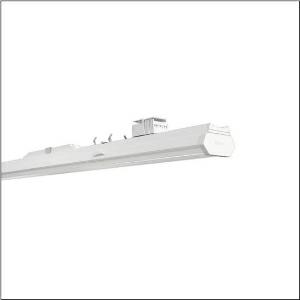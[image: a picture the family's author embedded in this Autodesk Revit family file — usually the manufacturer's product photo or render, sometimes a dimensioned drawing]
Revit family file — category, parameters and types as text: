
# Revit family: licross_r__11_protected_ho_51td12dn4fxm3s_901f
name_source: partatom
category: Lighting Fixtures
units: mm (PartAtom-declared; Revit-internal decimal feet)

## family parameters
Cut with Voids When Loaded = No
Host = Face
Light Source = No
Part Type = Normal
Room Calculation Point = No
Round Connector Dimension = Use Diameter
Shared = No

## types (1)
- --- (1 x LED, 970 lm, 7.4 W, 4000K)
    Apparent Load = 7 VA
    CIE Flux Codes = 70 91 97 98 100
    Color Rendering = 80
    Color Temperature = 4000K
    Default Elevation = 1800 mm
    Description = Licross® 11 Protected HO, luminaire insert, of sheet steel, galvanised, coil coated, white, length: 1.500mm, width: 90mm, height: 101mm, LED rated luminous flux: 15.270lm, light colour: 840, control gear: DALI 2 (for two DALI lines), with plug, 6-pole, with phase selection, for trunking rail, 14-core, mains connection: 220..240V, AC, 50/60Hz, rated input power: 91W, for trunking rail, 14-core, halogen-free wiring, for emergency light function, converter,control gear: single battery element, battery: LiFePO4, 9Ah, primary light control with lens, of plastic, primary optical cover: cover, of PMMA, light emission: direct distribution, primary light characteristic: symmetric, protection rating (complete): IP54, insulation class (complete): insulation class I (protective earthing), certification: CE, UKCA, protection symbol: D if used in an environment with non-conductive dust loads with corresponding accessories, impact resistance: IK06, permissible ambient temperature for indoor applications: +5..+30°C, standard: EN 60598-2-22, LABS conformity tested according to VDMA 24364:2018-05, reducing of maximum allowable ambient temperature of 5°C with ceiling mounting, corresponds to IFS (International Featured Standards) requirements for safety and quality in the food industry, packaging unit: 1 piece
    Height = 92 mm
    Lamp = 1 x LED
    Lamp Light Flux = 970 lm
    Lamp Power = 7.4 W
    Lamp count = 1
    Length = 1500 mm
    Luminous efficacy = 131 lm/W
    Manufacturer = Siteco
    ModVariant = No
    Model = 51TD12DN4FXM3S
    Mounting Place = Ceiling
    Mounting Type = Pendant
    Number of Poles = 1
    OnlyDefault = Yes
    Power Factor = 1
    Product Name = Licross® 11 Protected HO
    Product group = luminaire insert
    ProductGroupID = 902
    Protection Class = Protection class I
    Protection Degree = IP 54
    RLX_Detail_Level = 1
    RLX_Emergency_Light_Flux = 0 lm
    RLX_Emergency_Type = 0
    RLX_Emergency_Type_DB = No
    RlxData = <blob elided: 24913 chars, md5=604bb027>
    Socket = socket
    Standby Power = 0 W
    System Light Flux = 970 lm
    System Power = 7 W
    Type Comments = : emergency light operation: 3 h
    Type Image = l_1256145.jpg
    URL = http://relux.com
    VarID = @adj_090950
    Voltage = 0 V
    Weight = 0.00 kg
    Width = 88 mm

## geometry (parser evidence)
native form markers: Blend x4, Sweep x12
no freeform markers — native parametric forms only
